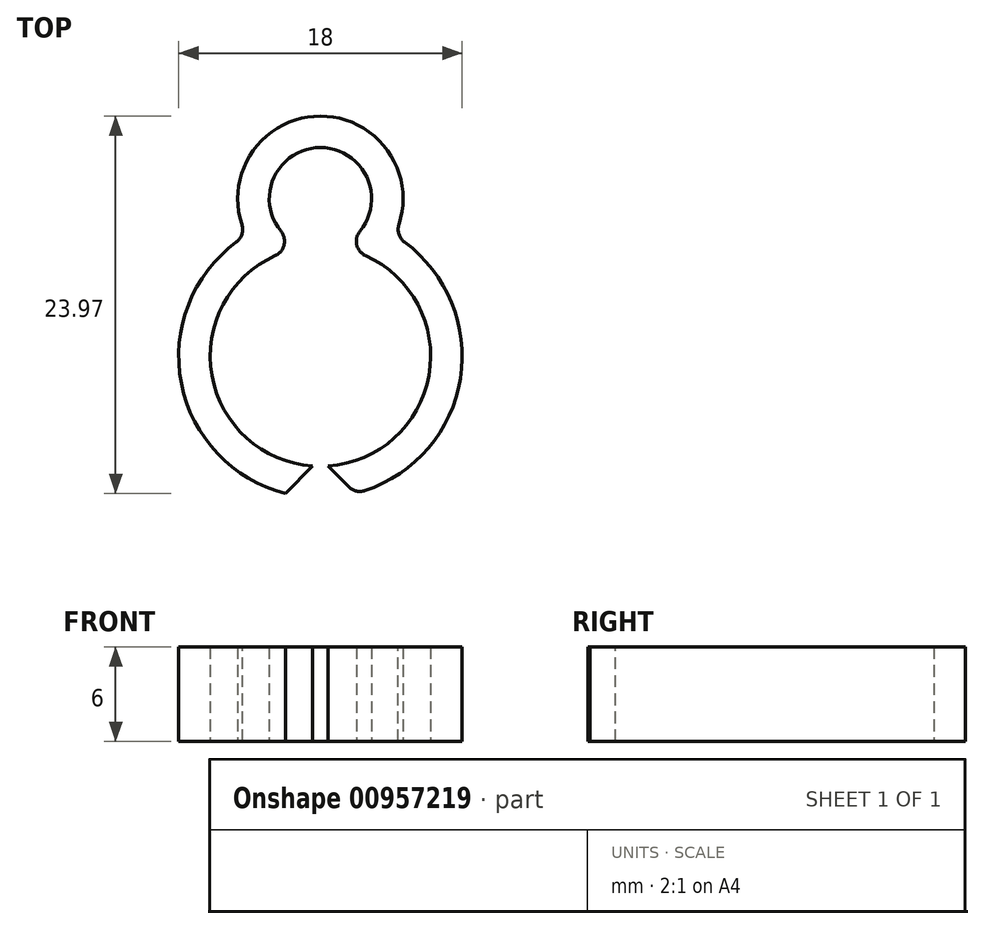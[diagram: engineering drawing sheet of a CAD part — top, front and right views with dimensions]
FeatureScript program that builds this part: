
annotation { "Feature Type Name" : "Feature", "Feature Type Description" : "" }
export const myFeature = defineFeature(function(context is Context, id is Id, definition is map)
    precondition{}
    {
        {
            var Q0;
            Q0=qCreatedBy(makeId("Top.planeOp"),FACE);
            var sketch = newSketch(context, id + "F0", { "sketchPlane" : qUnion([Q0])});
            skArc(sketch, "E0", {"start": v(-1.04, 6.92) * mm, "mid": v(0, -7) * mm, "end": v(1.04, 6.92) * mm});
            skArc(sketch, "E1", {"start": v(1.04, 6.92) * mm, "mid": v(0, 13.25) * mm, "end": v(-1.04, 6.92) * mm});
            skArc(sketch, "E2.0", {"start": v(4.7, 7.67) * mm, "mid": v(0, 15.25) * mm, "end": v(-4.7, 7.67) * mm});
            skArc(sketch, "E2.1", {"start": v(-4.7, 7.67) * mm, "mid": v(0, -9) * mm, "end": v(4.7, 7.67) * mm});
            skSolve(sketch);
        }
        {
            var Q0;
            Q0=makeQuery(id+"F0.imprint","IMPRINT",FACE,{"disambiguationData":[TD([[makeQuery(id+"F0.imprint","IMPRINT",EDGE,{"derivedFrom":sQuery(id+"F0.wireOp",EDGE,"E0")}),-1.0]])]});
            extrude(context, id + "F1", {"entities" : qUnion([Q0]), "depth" : 6 * mm, "offsetDistance" : 25 * mm});
        }
        {
            var Q0;
            Q0=makeQuery(id+"F1.opExtrude","CAP_FACE",FACE,{"disambiguationData":[OSD([sQuery(id+"F0.wireOp",EDGE,"E0"),sQuery(id+"F0.wireOp",EDGE,"E1"),sQuery(id+"F0.wireOp",EDGE,"E2.0"),sQuery(id+"F0.wireOp",EDGE,"E2.1")])],"isStart":false});
            var sketch = newSketch(context, id + "F2", { "sketchPlane" : qUnion([Q0])});
            skLineSegment(sketch, "E3", {"start": v(-0.5, -6.98) * mm, "end": v(0.5, -6.98) * mm});
            skLineSegment(sketch, "E4", {"start": v(0.5, -6.98) * mm, "end": v(2.5, -9) * mm});
            skLineSegment(sketch, "E5", {"start": v(2.5, -9) * mm, "end": v(-2.5, -9) * mm});
            skLineSegment(sketch, "E6", {"start": v(-2.5, -9) * mm, "end": v(-0.5, -6.98) * mm});
            skSolve(sketch);
        }
        {
            var Q0;
            {var subQ0=sQuery(id+"F2.wireOp",EDGE,"E4");var subQ1=makeQuery(id+"F1.opExtrude","CAP_EDGE",EDGE,{"disambiguationData":[OSD([sQuery(id+"F0.wireOp",EDGE,"E2.1")])],"isStart":false});var subQ2=makeQuery(id+"F2.imprint","INTERSECT",VERTEX,{"derivedFrom":[subQ1,subQ0]});Q0=makeQuery(id+"F2.imprint","IMPRINT",FACE,{"disambiguationData":[TD([[makeQuery(id+"F2.imprint","IMPRINT",EDGE,{"disambiguationData":[TD([[subQ2,1.0]])],"derivedFrom":subQ1}),1.0]])]});}
            extrude(context, id + "F3", {"entities" : qUnion([Q0]), "operationType" : NewBodyOperationType.REMOVE, "endBound" : BoundingType.THROUGH_ALL, "oppositeDirection" : true, "depth" : 25 * mm, "offsetDistance" : 25 * mm});
        }
        {
            var Q0;
            {var subQ0=sQuery(id+"F0.wireOp",EDGE,"E1");var subQ1=sQuery(id+"F0.wireOp",EDGE,"E0");Q0=makeQuery(id+"F1.opExtrude","SWEPT_EDGE",EDGE,{"disambiguationData":[OSD([subQ1,subQ0]),TDD([makeQuery(id+"F0.imprint","INTERSECT",VERTEX,{"disambiguationData":[OD(0.0)],"derivedFrom":[subQ1,subQ0]})])]});}
            var Q1;
            {var subQ0=sQuery(id+"F0.wireOp",EDGE,"E1");var subQ1=sQuery(id+"F0.wireOp",EDGE,"E0");Q1=makeQuery(id+"F1.opExtrude","SWEPT_EDGE",EDGE,{"disambiguationData":[OSD([subQ1,subQ0]),TDD([makeQuery(id+"F0.imprint","INTERSECT",VERTEX,{"disambiguationData":[OD(1.0)],"derivedFrom":[subQ1,subQ0]})])]});}
            var Q2;
            {var subQ0=sQuery(id+"F0.wireOp",EDGE,"E2.1");var subQ1=sQuery(id+"F0.wireOp",EDGE,"E2.0");Q2=makeQuery(id+"F1.opExtrude","SWEPT_EDGE",EDGE,{"disambiguationData":[OSD([subQ1,subQ0]),TDD([makeQuery(id+"F0.imprint","INTERSECT",VERTEX,{"disambiguationData":[OD(0.0)],"derivedFrom":[subQ1,subQ0]})])]});}
            var Q3;
            {var subQ0=sQuery(id+"F0.wireOp",EDGE,"E2.1");var subQ1=sQuery(id+"F0.wireOp",EDGE,"E2.0");Q3=makeQuery(id+"F1.opExtrude","SWEPT_EDGE",EDGE,{"disambiguationData":[OSD([subQ1,subQ0]),TDD([makeQuery(id+"F0.imprint","INTERSECT",VERTEX,{"disambiguationData":[OD(1.0)],"derivedFrom":[subQ1,subQ0]})])]});}
            var Q4;
            Q4=makeQuery(id+"F3.boolean.opBoolean","COPY",EDGE,{"derivedFrom":makeQuery(id+"F3.opExtrude","SWEPT_EDGE",EDGE,{"disambiguationData":[OSD([sQuery(id+"F0.wireOp",EDGE,"E2.1"),sQuery(id+"F2.wireOp",EDGE,"E4")])]})});
            var Q5;
            Q5=makeQuery(id+"F3.boolean.opBoolean","COPY",EDGE,{"derivedFrom":makeQuery(id+"F3.opExtrude","SWEPT_EDGE",EDGE,{"disambiguationData":[OSD([sQuery(id+"F0.wireOp",EDGE,"E2.1"),sQuery(id+"F2.wireOp",EDGE,"E6")])]})});
            fillet(context, id + "F4", {"entities" : qUnion([Q0, Q1, Q2, Q3, Q4, Q5]), "radius" : 1 * mm, "tangentPropagation" : true, "allowEdgeOverflow" : false});
        }
    });
